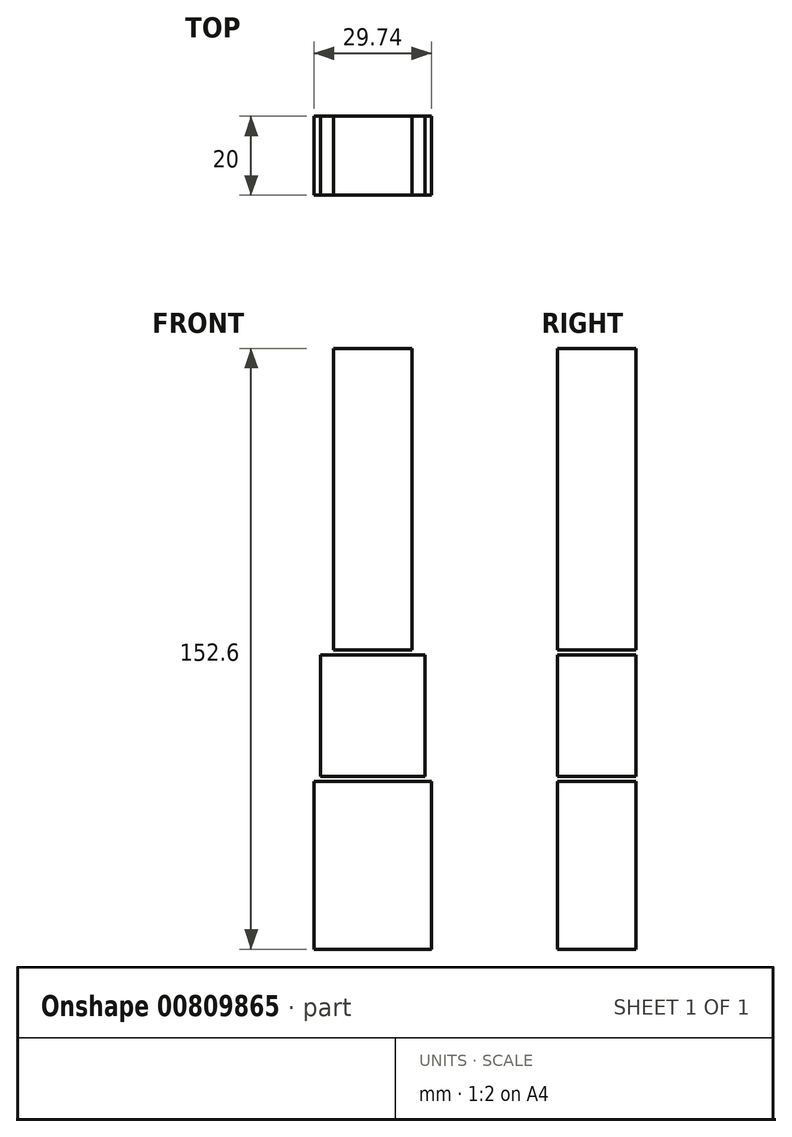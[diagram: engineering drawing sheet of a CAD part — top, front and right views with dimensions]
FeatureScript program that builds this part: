
annotation { "Feature Type Name" : "Feature", "Feature Type Description" : "" }
export const myFeature = defineFeature(function(context is Context, id is Id, definition is map)
    precondition{}
    {
        {
            var Q0;
            Q0=qCreatedBy(makeId("Front.planeOp"),FACE);
            var sketch = newSketch(context, id + "F0", { "sketchPlane" : qUnion([Q0])});
            skLineSegment(sketch, "E0.bottom", {"start": v(0, 0) * mm, "end": v(29.74, 0) * mm});
            skLineSegment(sketch, "E0.top", {"start": v(0, 42.67) * mm, "end": v(29.74, 42.67) * mm});
            skLineSegment(sketch, "E0.left", {"start": v(0, 0) * mm, "end": v(0, 42.67) * mm});
            skLineSegment(sketch, "E0.right", {"start": v(29.74, 0) * mm, "end": v(29.74, 42.67) * mm});
            skLineSegment(sketch, "E1.bottom", {"start": v(1.55, 43.94) * mm, "end": v(28.2, 43.94) * mm});
            skLineSegment(sketch, "E1.top", {"start": v(1.55, 74.78) * mm, "end": v(28.2, 74.78) * mm});
            skLineSegment(sketch, "E1.left", {"start": v(1.55, 43.94) * mm, "end": v(1.55, 74.78) * mm});
            skLineSegment(sketch, "E1.right", {"start": v(28.2, 43.94) * mm, "end": v(28.2, 74.78) * mm});
            skLineSegment(sketch, "E2.bottom", {"start": v(4.91, 76.05) * mm, "end": v(24.83, 76.05) * mm});
            skLineSegment(sketch, "E2.top", {"start": v(4.91, 152.6) * mm, "end": v(24.83, 152.6) * mm});
            skLineSegment(sketch, "E2.left", {"start": v(4.91, 76.05) * mm, "end": v(4.91, 152.6) * mm});
            skLineSegment(sketch, "E2.right", {"start": v(24.83, 76.05) * mm, "end": v(24.83, 152.6) * mm});
            skPoint(sketch, "E3", {"position": v(14.87, 0) * mm});
            skPoint(sketch, "E4", {"position": v(14.87, 43.94) * mm});
            skPoint(sketch, "E5", {"position": v(14.87, 76.05) * mm});
            skLineSegment(sketch, "E6", {"start": v(14.87, 0) * mm, "end": v(14.87, 180.09) * mm, "construction": true});
            skSolve(sketch);
        }
        {
            var Q0;
            Q0=makeQuery(id+"F0.imprint","IMPRINT",FACE,{"disambiguationData":[TD([[makeQuery(id+"F0.imprint","IMPRINT",EDGE,{"derivedFrom":sQuery(id+"F0.wireOp",EDGE,"E0.bottom")}),1.0]])]});
            var Q1;
            Q1=makeQuery(id+"F0.imprint","IMPRINT",FACE,{"disambiguationData":[TD([[makeQuery(id+"F0.imprint","IMPRINT",EDGE,{"derivedFrom":sQuery(id+"F0.wireOp",EDGE,"E1.bottom")}),1.0]])]});
            var Q2;
            Q2=makeQuery(id+"F0.imprint","IMPRINT",FACE,{"disambiguationData":[TD([[makeQuery(id+"F0.imprint","IMPRINT",EDGE,{"derivedFrom":sQuery(id+"F0.wireOp",EDGE,"E2.bottom")}),1.0]])]});
            extrude(context, id + "F1", {"entities" : qUnion([Q0, Q1, Q2]), "oppositeDirection" : true, "depth" : 20 * mm, "offsetDistance" : 25.4 * mm});
        }
    });
